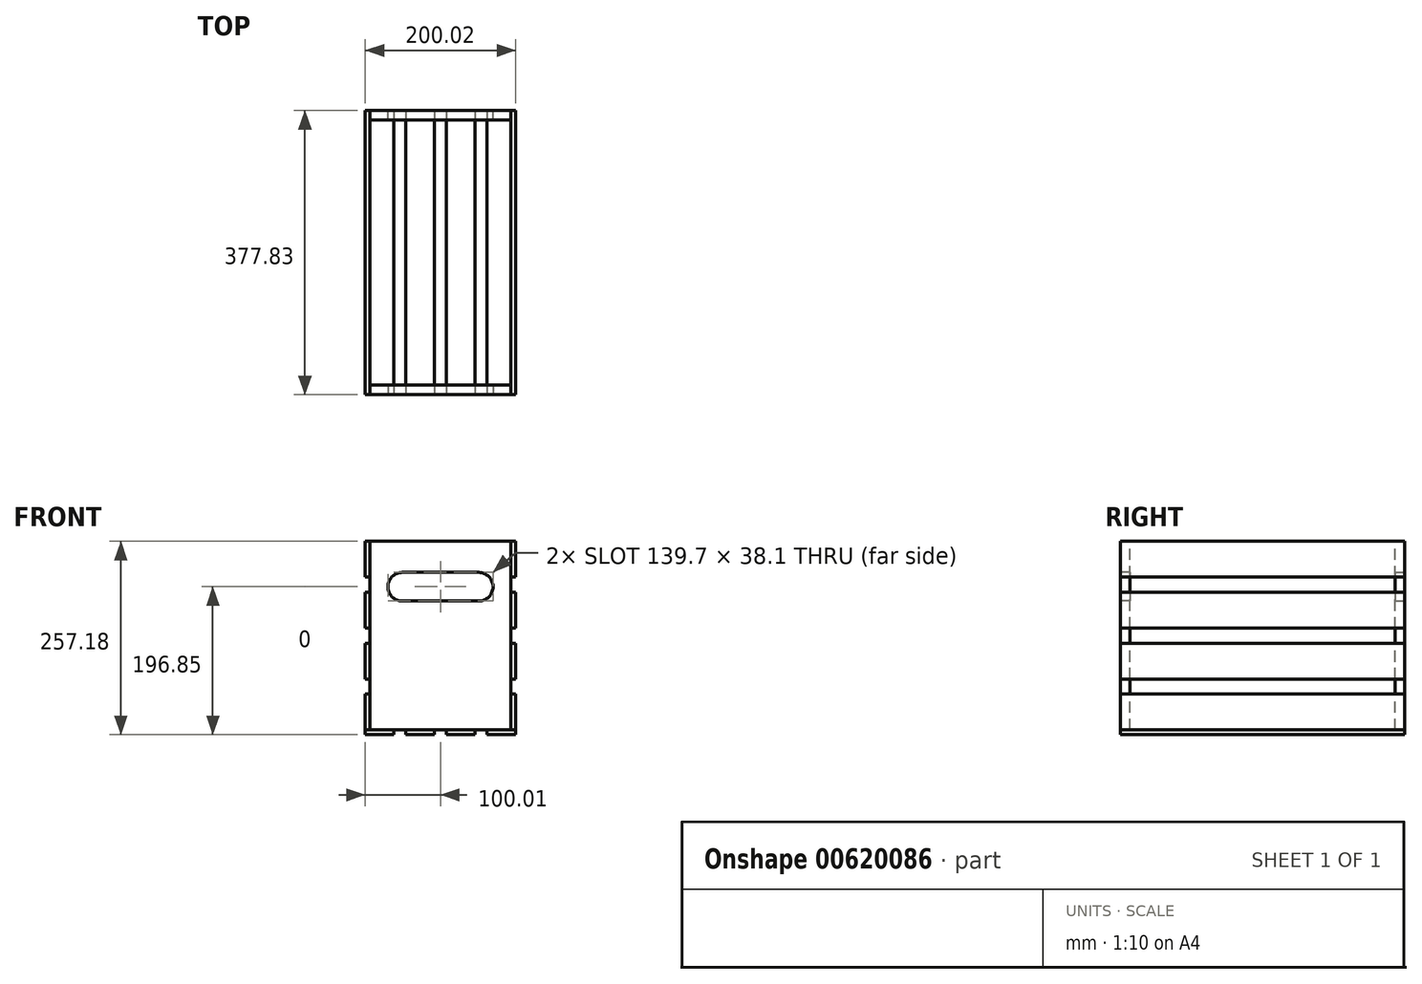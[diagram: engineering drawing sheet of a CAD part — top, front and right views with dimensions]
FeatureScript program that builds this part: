
annotation { "Feature Type Name" : "Feature", "Feature Type Description" : "" }
export const myFeature = defineFeature(function(context is Context, id is Id, definition is map)
    precondition{}
    {
        {
            var Q0;
            Q0=qCreatedBy(makeId("Front.planeOp"),FACE);
            var sketch = newSketch(context, id + "F0", { "sketchPlane" : qUnion([Q0])});
            skLineSegment(sketch, "E0", {"start": v(-93.66, 0) * mm, "end": v(93.66, 0) * mm});
            skLineSegment(sketch, "E1", {"start": v(93.66, 0) * mm, "end": v(93.66, 250.82) * mm});
            skLineSegment(sketch, "E2", {"start": v(93.66, 250.83) * mm, "end": v(-93.66, 250.83) * mm});
            skLineSegment(sketch, "E3", {"start": v(-93.66, 250.82) * mm, "end": v(-93.66, 0) * mm});
            skArc(sketch, "E4", {"start": v(-50.8, 209.55) * mm, "mid": v(-69.85, 190.5) * mm, "end": v(-50.8, 171.45) * mm});
            skLineSegment(sketch, "E5", {"start": v(0, 0) * mm, "end": v(0, 250.83) * mm, "construction": true});
            skArc(sketch, "E6.MirrorC", {"start": v(50.8, 209.55) * mm, "mid": v(69.85, 190.5) * mm, "end": v(50.8, 171.45) * mm});
            skLineSegment(sketch, "E7", {"start": v(-50.8, 209.55) * mm, "end": v(50.8, 209.55) * mm});
            skLineSegment(sketch, "E8", {"start": v(50.8, 171.45) * mm, "end": v(-50.8, 171.45) * mm});
            skSolve(sketch);
        }
        {
            var Q0;
            Q0 = qSketchRegion(id + "F0", true);
            extrude(context, id + "F1", {"entities" : qUnion([Q0]), "oppositeDirection" : true, "depth" : 12.7 * mm, "offsetDistance" : 25.4 * mm});
        }
        {
            var Q0;
            Q0=makeQuery(id+"F1.opExtrude","CAP_FACE",FACE,{"disambiguationData":[OSD([sQuery(id+"F0.wireOp",EDGE,"E0"),sQuery(id+"F0.wireOp",EDGE,"E1"),sQuery(id+"F0.wireOp",EDGE,"E2"),sQuery(id+"F0.wireOp",EDGE,"E3"),sQuery(id+"F0.wireOp",EDGE,"E4"),sQuery(id+"F0.wireOp",EDGE,"E6.MirrorC"),sQuery(id+"F0.wireOp",EDGE,"E7"),sQuery(id+"F0.wireOp",EDGE,"E8")])],"isStart":true});
            cPlane(context, id + "F2", {"entities" : qUnion([Q0]), "cplaneType" : CPlaneType.OFFSET, "offset" : 188.9 * mm, "oppositeDirection" : true, "width" : 152.4 * mm, "height" : 152.4 * mm});
        }
        {
            var Q0;
            Q0=makeQuery(id+"F1.opExtrude","SWEPT_BODY",BODY,{"disambiguationData":[OSD([sQuery(id+"F0.wireOp",EDGE,"E0"),sQuery(id+"F0.wireOp",EDGE,"E1"),sQuery(id+"F0.wireOp",EDGE,"E2"),sQuery(id+"F0.wireOp",EDGE,"E3"),sQuery(id+"F0.wireOp",EDGE,"E4"),sQuery(id+"F0.wireOp",EDGE,"E6.MirrorC"),sQuery(id+"F0.wireOp",EDGE,"E7"),sQuery(id+"F0.wireOp",EDGE,"E8")])]});
            var Q1;
            Q1=qCreatedBy(id+"F2.planeOp",FACE);
            mirror(context, id + "F3", {"entities" : qUnion([Q0]), "mirrorPlane" : qUnion([Q1])});
        }
        {
            var Q0;
            Q0=makeQuery(id+"F1.opExtrude","CAP_FACE",FACE,{"disambiguationData":[OSD([sQuery(id+"F0.wireOp",EDGE,"E0"),sQuery(id+"F0.wireOp",EDGE,"E1"),sQuery(id+"F0.wireOp",EDGE,"E2"),sQuery(id+"F0.wireOp",EDGE,"E3"),sQuery(id+"F0.wireOp",EDGE,"E4"),sQuery(id+"F0.wireOp",EDGE,"E6.MirrorC"),sQuery(id+"F0.wireOp",EDGE,"E7"),sQuery(id+"F0.wireOp",EDGE,"E8")])],"isStart":true});
            var sketch = newSketch(context, id + "F4", { "sketchPlane" : qUnion([Q0])});
            skLineSegment(sketch, "E9.0", {"start": v(93.66, 0) * mm, "end": v(93.66, 47.63) * mm});
            skLineSegment(sketch, "E9.1", {"start": v(-93.66, 0) * mm, "end": v(93.66, 0) * mm});
            skLineSegment(sketch, "E10", {"start": v(93.66, 250.83) * mm, "end": v(100.01, 250.83) * mm});
            skLineSegment(sketch, "E11", {"start": v(100.01, 250.82) * mm, "end": v(100.01, 203.2) * mm});
            skLineSegment(sketch, "E12", {"start": v(100.01, 0) * mm, "end": v(93.66, 0) * mm});
            skLineSegment(sketch, "E13", {"start": v(93.66, 203.2) * mm, "end": v(100.01, 203.2) * mm});
            skLineSegment(sketch, "E14", {"start": v(93.66, 183.1) * mm, "end": v(100.01, 183.1) * mm});
            skLineSegment(sketch, "E15", {"start": v(93.66, 135.47) * mm, "end": v(100.01, 135.47) * mm});
            skLineSegment(sketch, "E16", {"start": v(93.66, 115.36) * mm, "end": v(100.01, 115.36) * mm});
            skLineSegment(sketch, "E17", {"start": v(93.66, 67.73) * mm, "end": v(100.01, 67.73) * mm});
            skLineSegment(sketch, "E18", {"start": v(93.66, 47.63) * mm, "end": v(100.01, 47.63) * mm});
            skLineSegment(sketch, "E19.trimOffspring", {"start": v(93.66, 67.73) * mm, "end": v(93.66, 115.36) * mm});
            skLineSegment(sketch, "E20.trimOffspring", {"start": v(100.01, 47.62) * mm, "end": v(100.01, 0) * mm});
            skLineSegment(sketch, "E21.trimOffspring", {"start": v(93.66, 135.47) * mm, "end": v(93.66, 183.1) * mm});
            skLineSegment(sketch, "E22.trimOffspring", {"start": v(100.01, 115.36) * mm, "end": v(100.01, 67.73) * mm});
            skLineSegment(sketch, "E23.trimOffspring", {"start": v(93.66, 203.2) * mm, "end": v(93.66, 250.82) * mm});
            skLineSegment(sketch, "E24.trimOffspring", {"start": v(100.01, 183.1) * mm, "end": v(100.01, 135.47) * mm});
            skLineSegment(sketch, "E25", {"start": v(100.01, 203.2) * mm, "end": v(100.01, 183.1) * mm, "construction": true});
            skLineSegment(sketch, "E26", {"start": v(100.01, 135.47) * mm, "end": v(100.01, 115.36) * mm, "construction": true});
            skLineSegment(sketch, "E27", {"start": v(100.01, 67.73) * mm, "end": v(100.01, 47.63) * mm, "construction": true});
            skSolve(sketch);
        }
        {
            var Q0;
            Q0 = qSketchRegion(id + "F4", true);
            var Q1;
            Q1=makeQuery(id+"F3.opPattern","COPY",FACE,{"derivedFrom":makeQuery(id+"F1.opExtrude","CAP_FACE",FACE,{"disambiguationData":[OSD([sQuery(id+"F0.wireOp",EDGE,"E0"),sQuery(id+"F0.wireOp",EDGE,"E1"),sQuery(id+"F0.wireOp",EDGE,"E2"),sQuery(id+"F0.wireOp",EDGE,"E3"),sQuery(id+"F0.wireOp",EDGE,"E4"),sQuery(id+"F0.wireOp",EDGE,"E6.MirrorC"),sQuery(id+"F0.wireOp",EDGE,"E7"),sQuery(id+"F0.wireOp",EDGE,"E8")])],"isStart":true}),"instanceName":"1"});
            extrude(context, id + "F5", {"entities" : qUnion([Q0]), "endBound" : BoundingType.UP_TO_SURFACE, "oppositeDirection" : true, "depth" : 25.4 * mm, "endBoundEntityFace" : qUnion([Q1]), "offsetDistance" : 25.4 * mm});
        }
        {
            var Q0;
            Q0=makeQuery(id+"F5.opExtrude","SWEPT_BODY",BODY,{"disambiguationData":[OSD([sQuery(id+"F4.wireOp",EDGE,"E10"),sQuery(id+"F4.wireOp",EDGE,"E11"),sQuery(id+"F4.wireOp",EDGE,"E13"),sQuery(id+"F4.wireOp",EDGE,"E23.trimOffspring")])]});
            var Q1;
            Q1=makeQuery(id+"F5.opExtrude","SWEPT_BODY",BODY,{"disambiguationData":[OSD([sQuery(id+"F4.wireOp",EDGE,"E14"),sQuery(id+"F4.wireOp",EDGE,"E15"),sQuery(id+"F4.wireOp",EDGE,"E21.trimOffspring"),sQuery(id+"F4.wireOp",EDGE,"E24.trimOffspring")])]});
            var Q2;
            Q2=makeQuery(id+"F5.opExtrude","SWEPT_BODY",BODY,{"disambiguationData":[OSD([sQuery(id+"F4.wireOp",EDGE,"E9.0"),sQuery(id+"F4.wireOp",EDGE,"E12"),sQuery(id+"F4.wireOp",EDGE,"E18"),sQuery(id+"F4.wireOp",EDGE,"E20.trimOffspring")])]});
            var Q3;
            Q3=makeQuery(id+"F5.opExtrude","SWEPT_BODY",BODY,{"disambiguationData":[OSD([sQuery(id+"F4.wireOp",EDGE,"E16"),sQuery(id+"F4.wireOp",EDGE,"E17"),sQuery(id+"F4.wireOp",EDGE,"E19.trimOffspring"),sQuery(id+"F4.wireOp",EDGE,"E22.trimOffspring")])]});
            var Q4;
            Q4=qCreatedBy(makeId("Right.planeOp"),FACE);
            mirror(context, id + "F6", {"entities" : qUnion([Q0, Q1, Q2, Q3]), "mirrorPlane" : qUnion([Q4])});
        }
        {
            var Q0;
            Q0=makeQuery(id+"F1.opExtrude","CAP_FACE",FACE,{"disambiguationData":[OSD([sQuery(id+"F0.wireOp",EDGE,"E0"),sQuery(id+"F0.wireOp",EDGE,"E1"),sQuery(id+"F0.wireOp",EDGE,"E2"),sQuery(id+"F0.wireOp",EDGE,"E3"),sQuery(id+"F0.wireOp",EDGE,"E4"),sQuery(id+"F0.wireOp",EDGE,"E6.MirrorC"),sQuery(id+"F0.wireOp",EDGE,"E7"),sQuery(id+"F0.wireOp",EDGE,"E8")])],"isStart":true});
            var sketch = newSketch(context, id + "F7", { "sketchPlane" : qUnion([Q0])});
            skLineSegment(sketch, "E28.0", {"start": v(-93.66, 0) * mm, "end": v(-61.91, 0) * mm});
            skLineSegment(sketch, "E28.1", {"start": v(100.01, 0) * mm, "end": v(93.66, 0) * mm});
            skLineSegment(sketch, "E29.0", {"start": v(-100.01, 0) * mm, "end": v(-93.66, 0) * mm});
            skLineSegment(sketch, "E30", {"start": v(-100.01, 0) * mm, "end": v(-100.01, -6.35) * mm});
            skLineSegment(sketch, "E31", {"start": v(-100.01, -6.35) * mm, "end": v(-61.91, -6.35) * mm});
            skLineSegment(sketch, "E32", {"start": v(100.01, -6.35) * mm, "end": v(100.01, 0) * mm});
            skLineSegment(sketch, "E33", {"start": v(-61.91, 0) * mm, "end": v(-61.91, -6.35) * mm});
            skLineSegment(sketch, "E34", {"start": v(-46.04, 0) * mm, "end": v(-46.04, -6.35) * mm});
            skLineSegment(sketch, "E35", {"start": v(-7.94, 0) * mm, "end": v(-7.94, -6.35) * mm});
            skLineSegment(sketch, "E36", {"start": v(7.94, 0) * mm, "end": v(7.94, -6.35) * mm});
            skLineSegment(sketch, "E37", {"start": v(46.04, 0) * mm, "end": v(46.04, -6.35) * mm});
            skLineSegment(sketch, "E38", {"start": v(61.91, 0) * mm, "end": v(61.91, -6.35) * mm});
            skLineSegment(sketch, "E39.trimOffspring", {"start": v(61.91, 0) * mm, "end": v(93.66, 0) * mm});
            skLineSegment(sketch, "E40.trimOffspring", {"start": v(61.91, -6.35) * mm, "end": v(100.01, -6.35) * mm});
            skLineSegment(sketch, "E41.trimOffspring", {"start": v(7.94, 0) * mm, "end": v(46.04, 0) * mm});
            skLineSegment(sketch, "E42.trimOffspring", {"start": v(7.94, -6.35) * mm, "end": v(46.04, -6.35) * mm});
            skLineSegment(sketch, "E43.trimOffspring", {"start": v(-46.04, 0) * mm, "end": v(-7.94, 0) * mm});
            skLineSegment(sketch, "E44.trimOffspring", {"start": v(-46.04, -6.35) * mm, "end": v(-7.94, -6.35) * mm});
            skLineSegment(sketch, "E45", {"start": v(-61.91, -6.35) * mm, "end": v(-46.04, -6.35) * mm, "construction": true});
            skLineSegment(sketch, "E46", {"start": v(-7.94, -6.35) * mm, "end": v(7.94, -6.35) * mm, "construction": true});
            skLineSegment(sketch, "E47", {"start": v(46.04, -6.35) * mm, "end": v(61.91, -6.35) * mm, "construction": true});
            skSolve(sketch);
        }
        {
            var Q0;
            Q0 = qSketchRegion(id + "F7", true);
            var Q1;
            Q1=makeQuery(id+"F3.opPattern","COPY",FACE,{"derivedFrom":makeQuery(id+"F1.opExtrude","CAP_FACE",FACE,{"disambiguationData":[OSD([sQuery(id+"F0.wireOp",EDGE,"E0"),sQuery(id+"F0.wireOp",EDGE,"E1"),sQuery(id+"F0.wireOp",EDGE,"E2"),sQuery(id+"F0.wireOp",EDGE,"E3"),sQuery(id+"F0.wireOp",EDGE,"E4"),sQuery(id+"F0.wireOp",EDGE,"E6.MirrorC"),sQuery(id+"F0.wireOp",EDGE,"E7"),sQuery(id+"F0.wireOp",EDGE,"E8")])],"isStart":true}),"instanceName":"1"});
            extrude(context, id + "F8", {"entities" : qUnion([Q0]), "endBound" : BoundingType.UP_TO_SURFACE, "oppositeDirection" : true, "depth" : 25.4 * mm, "endBoundEntityFace" : qUnion([Q1]), "offsetDistance" : 25.4 * mm});
        }
    });
